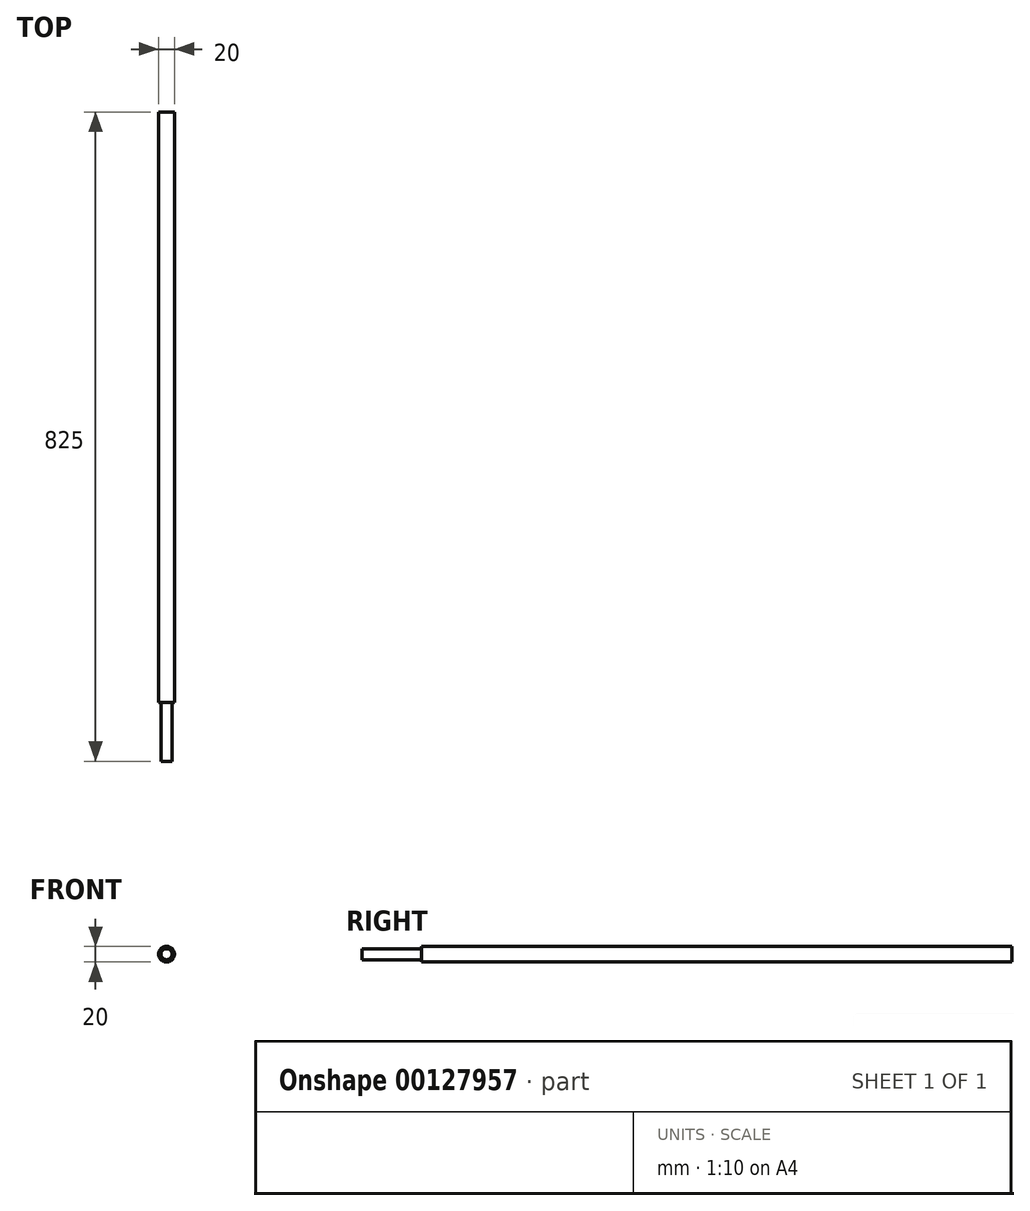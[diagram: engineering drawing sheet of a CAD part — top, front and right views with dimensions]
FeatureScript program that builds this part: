
annotation { "Feature Type Name" : "Feature", "Feature Type Description" : "" }
export const myFeature = defineFeature(function(context is Context, id is Id, definition is map)
    precondition{}
    {
        {
            var Q0;
            Q0=qCreatedBy(makeId("Front.planeOp"),FACE);
            var sketch = newSketch(context, id + "F0", { "sketchPlane" : qUnion([Q0])});
            skCircle(sketch, "E0", {"center": v(0, 0) * mm, "radius": 7 * mm});
            skSolve(sketch);
        }
        {
            var Q0;
            Q0=makeQuery(id+"F0.imprint","IMPRINT",FACE,{"disambiguationData":[TD([[makeQuery(id+"F0.imprint","IMPRINT",EDGE,{"derivedFrom":sQuery(id+"F0.wireOp",EDGE,"E0")}),1.0]])]});
            extrude(context, id + "F1", {"entities" : qUnion([Q0]), "depth" : 75 * mm});
        }
        {
            var Q0;
            Q0=makeQuery(id+"F1.opExtrude","CAP_FACE",FACE,{"disambiguationData":[OSD([sQuery(id+"F0.wireOp",EDGE,"E0")])],"isStart":true});
            var sketch = newSketch(context, id + "F2", { "sketchPlane" : qUnion([Q0])});
            skCircle(sketch, "E1", {"center": v(0, 0) * mm, "radius": 10 * mm});
            skSolve(sketch);
        }
        {
            var Q0;
            Q0=makeQuery(id+"F2.imprint","IMPRINT",FACE,{"disambiguationData":[TD([[makeQuery(id+"F2.imprint","IMPRINT",EDGE,{"derivedFrom":sQuery(id+"F2.wireOp",EDGE,"E1")}),1.0]])]});
            var Q1;
            Q1=makeQuery(id+"F2.imprint","IMPRINT",FACE,{"disambiguationData":[TD([[makeQuery(id+"F2.imprint","IMPRINT",EDGE,{"derivedFrom":makeQuery(id+"F1.opExtrude","CAP_EDGE",EDGE,{"disambiguationData":[OSD([sQuery(id+"F0.wireOp",EDGE,"E0")])],"isStart":true})}),-1.0]])]});
            extrude(context, id + "F3", {"entities" : qUnion([Q0, Q1]), "operationType" : NewBodyOperationType.ADD, "depth" : 750 * mm});
        }
    });
